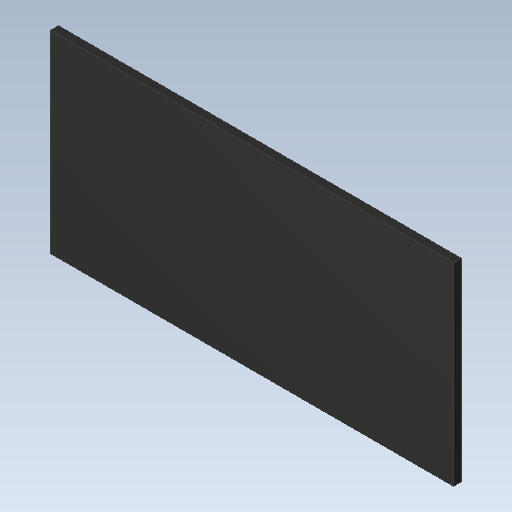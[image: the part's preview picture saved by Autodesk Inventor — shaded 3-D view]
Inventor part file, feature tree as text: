
AUTODESK INVENTOR PART (.ipt)
format: ipt  version: 2023 (Build 270158000, 158)  size: 92,160 bytes
history: imported  units: in
note: dims shown in document units (in); Inventor stores cm internally (conversion verified against a paired STEP export)
features: imported_body x1
ambient origin geometry x8: Origin, YZ Plane, XZ Plane, XY Plane, X Axis, Y Axis, Z Axis, Center Point
bodies: Solid1 (imported_parasolid), Body1 (imported_parasolid)
feature tree (1):
  imported_body  NMx_Import_Brep_tag  [imported B-rep: ~6 faces, bbox_mm=[5.1816, 2.4892, 0.1]]
